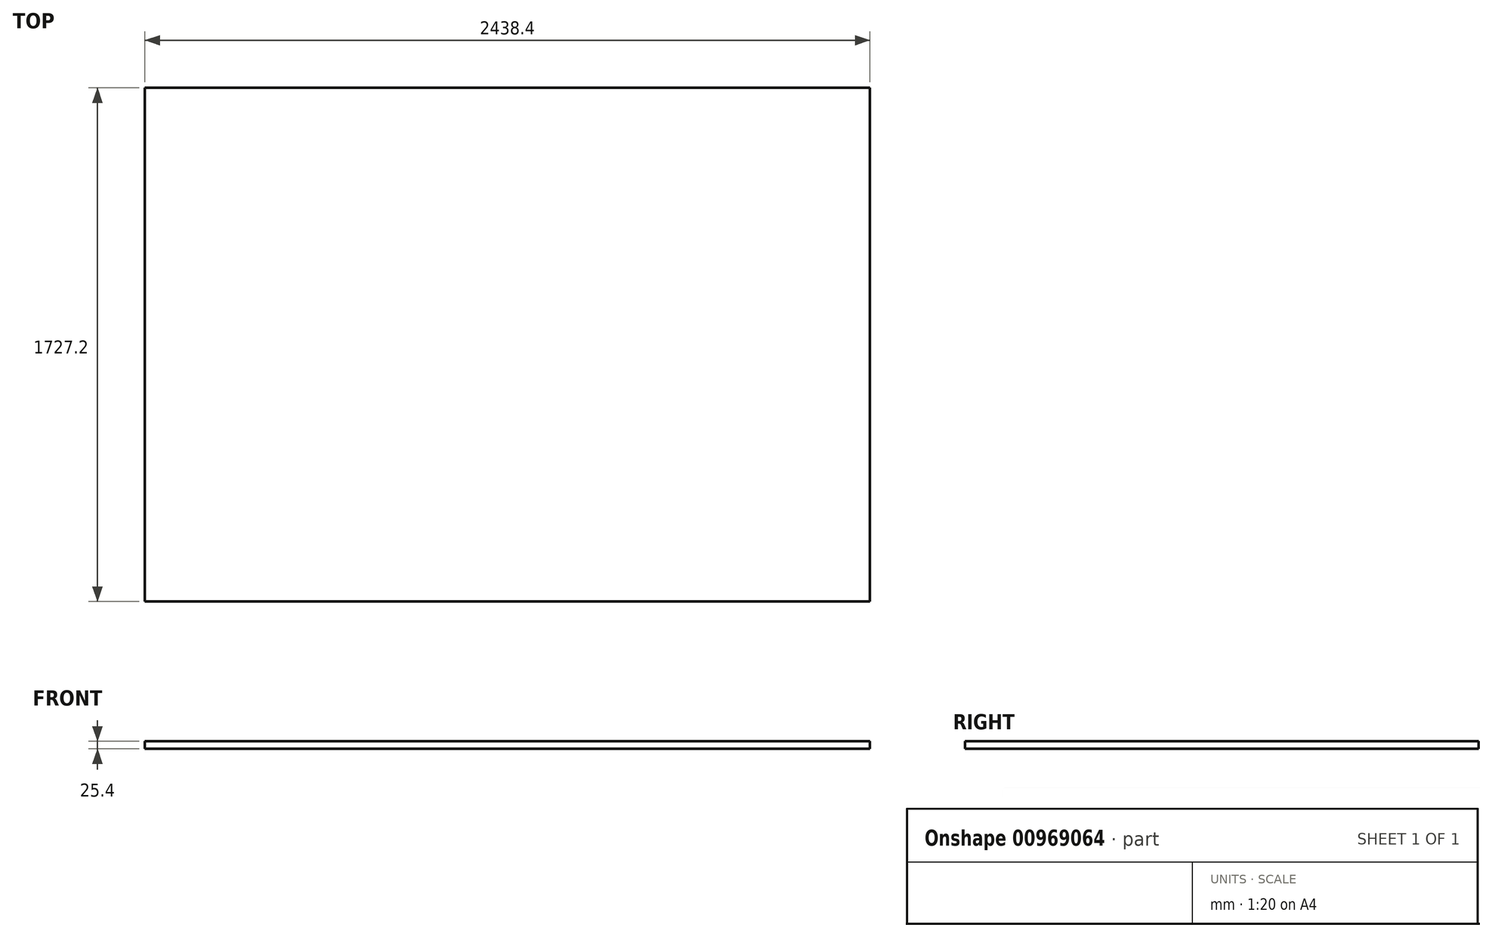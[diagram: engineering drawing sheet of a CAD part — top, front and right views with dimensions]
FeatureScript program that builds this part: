
annotation { "Feature Type Name" : "Feature", "Feature Type Description" : "" }
export const myFeature = defineFeature(function(context is Context, id is Id, definition is map)
    precondition{}
    {
        {
            var Q0;
            Q0=qCreatedBy(makeId("Top.planeOp"),FACE);
            var sketch = newSketch(context, id + "F0", { "sketchPlane" : qUnion([Q0])});
            skLineSegment(sketch, "E0.bottom", {"start": v(0, 0) * mm, "end": v(2438.4, 0) * mm});
            skLineSegment(sketch, "E0.top", {"start": v(0, -1727.2) * mm, "end": v(2438.4, -1727.2) * mm});
            skLineSegment(sketch, "E0.left", {"start": v(0, 0) * mm, "end": v(0, -1727.2) * mm});
            skLineSegment(sketch, "E0.right", {"start": v(2438.4, 0) * mm, "end": v(2438.4, -1727.2) * mm});
            skSolve(sketch);
        }
        {
            var Q0;
            Q0=makeQuery(id+"F0.imprint","IMPRINT",FACE,{"disambiguationData":[TD([[makeQuery(id+"F0.imprint","IMPRINT",EDGE,{"derivedFrom":sQuery(id+"F0.wireOp",EDGE,"E0.bottom")}),-1.0]])]});
            extrude(context, id + "F1", {"entities" : qUnion([Q0]), "depth" : 25.4 * mm, "offsetDistance" : 25.4 * mm});
        }
    });
